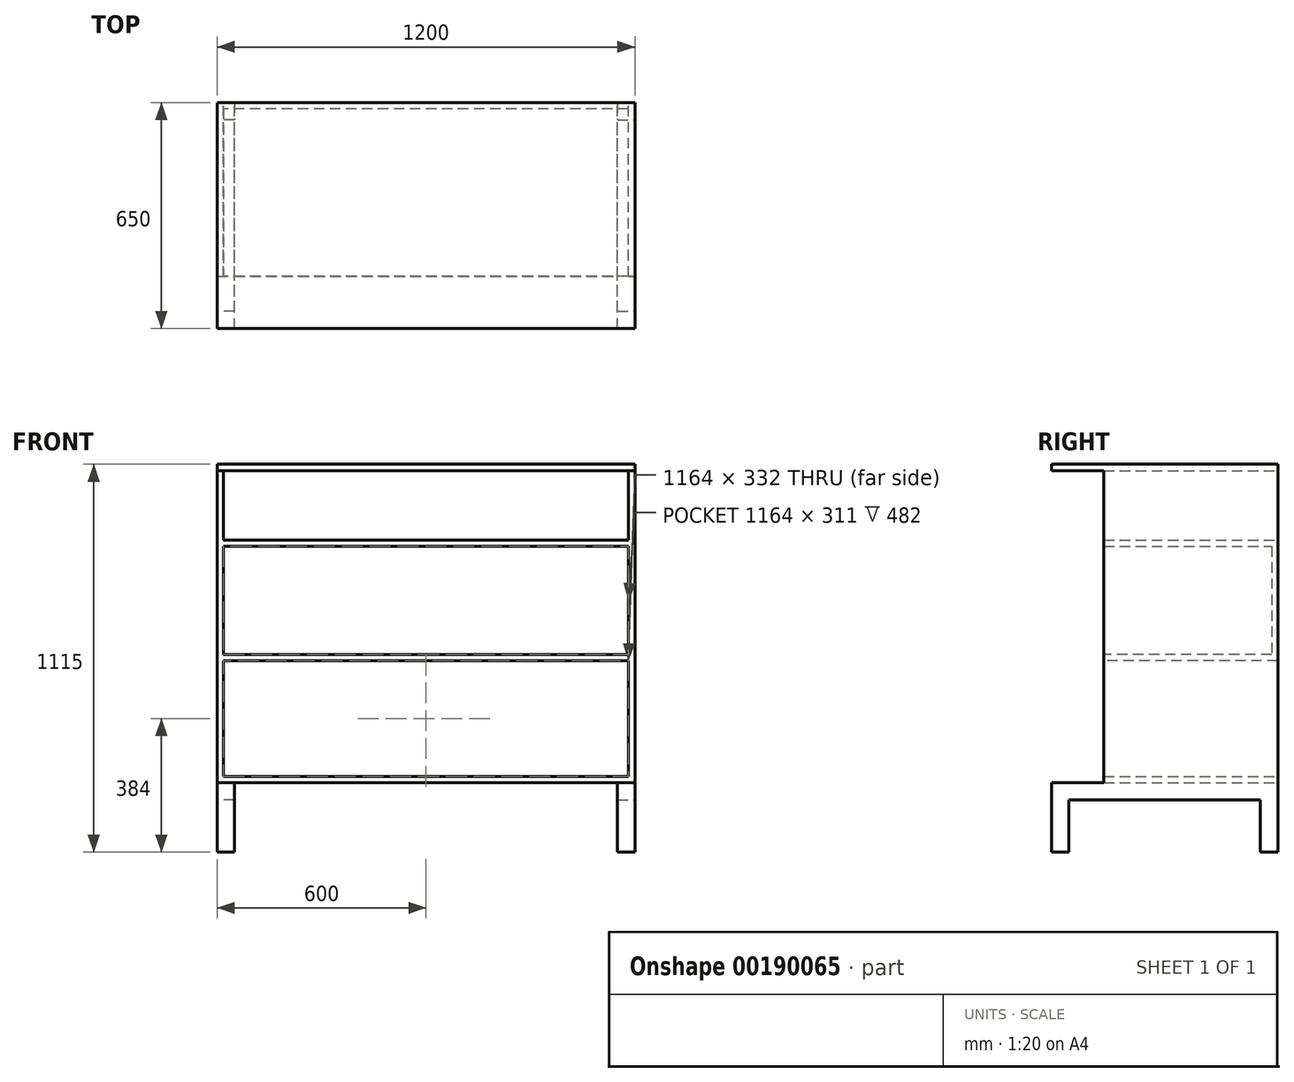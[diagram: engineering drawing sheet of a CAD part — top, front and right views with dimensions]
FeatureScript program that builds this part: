
annotation { "Feature Type Name" : "Feature", "Feature Type Description" : "" }
export const myFeature = defineFeature(function(context is Context, id is Id, definition is map)
    precondition{}
    {
        {
            var Q0;
            Q0=qCreatedBy(makeId("Front.planeOp"),FACE);
            var sketch = newSketch(context, id + "F0", { "sketchPlane" : qUnion([Q0])});
            skLineSegment(sketch, "E0.bottom", {"start": v(-600, 1115) * mm, "end": v(0, 1115) * mm});
            skLineSegment(sketch, "E0.left", {"start": v(-600, 1115) * mm, "end": v(-600, 200) * mm});
            skLineSegment(sketch, "E0.right", {"start": v(0, 1115) * mm, "end": v(0, 1097) * mm});
            skLineSegment(sketch, "E1", {"start": v(-600, 200) * mm, "end": v(0, 200) * mm});
            skLineSegment(sketch, "E2", {"start": v(0, 200) * mm, "end": v(0, 218) * mm});
            skLineSegment(sketch, "E3", {"start": v(0, 218) * mm, "end": v(-582, 218) * mm});
            skLineSegment(sketch, "E4", {"start": v(-582, 218) * mm, "end": v(-582, 1097) * mm});
            skLineSegment(sketch, "E5", {"start": v(-582, 1097) * mm, "end": v(0, 1097) * mm});
            skSolve(sketch);
        }
        {
            var Q0;
            Q0 = qSketchRegion(id + "F0", true);
            extrude(context, id + "F1", {"entities" : qUnion([Q0]), "depth" : 500 * mm});
        }
        {
            var Q0;
            Q0=qCreatedBy(makeId("Front.planeOp"),FACE);
            cPlane(context, id + "F2", {"entities" : qUnion([Q0]), "cplaneType" : CPlaneType.OFFSET, "offset" : 0 * mm, "oppositeDirection" : true, "width" : 150 * mm, "height" : 150 * mm});
        }
        {
            var Q0;
            Q0=qCreatedBy(id+"F2.planeOp",FACE);
            var sketch = newSketch(context, id + "F3", { "sketchPlane" : qUnion([Q0])});
            skLineSegment(sketch, "E6.bottom", {"start": v(-600, 200) * mm, "end": v(-550, 200) * mm});
            skLineSegment(sketch, "E6.top", {"start": v(-600, 150) * mm, "end": v(-550, 150) * mm});
            skLineSegment(sketch, "E6.left", {"start": v(-600, 200) * mm, "end": v(-600, 150) * mm});
            skLineSegment(sketch, "E6.right", {"start": v(-550, 200) * mm, "end": v(-550, 150) * mm});
            skSolve(sketch);
        }
        {
            var Q0;
            Q0 = qSketchRegion(id + "F3", true);
            extrude(context, id + "F4", {"entities" : qUnion([Q0]), "operationType" : NewBodyOperationType.ADD, "depth" : 650 * mm});
        }
        {
            var Q0;
            Q0=qCreatedBy(makeId("Top.planeOp"),FACE);
            var sketch = newSketch(context, id + "F5", { "sketchPlane" : qUnion([Q0])});
            skLineSegment(sketch, "E7.bottom", {"start": v(-600, 0) * mm, "end": v(-550, 0) * mm});
            skLineSegment(sketch, "E7.top", {"start": v(-600, -50) * mm, "end": v(-550, -50) * mm});
            skLineSegment(sketch, "E7.left", {"start": v(-600, 0) * mm, "end": v(-600, -50) * mm});
            skLineSegment(sketch, "E7.right", {"start": v(-550, 0) * mm, "end": v(-550, -50) * mm});
            skLineSegment(sketch, "E8.bottom", {"start": v(-600, -650) * mm, "end": v(-550, -650) * mm});
            skLineSegment(sketch, "E8.top", {"start": v(-600, -600) * mm, "end": v(-550, -600) * mm});
            skLineSegment(sketch, "E8.left", {"start": v(-600, -650) * mm, "end": v(-600, -600) * mm});
            skLineSegment(sketch, "E8.right", {"start": v(-550, -650) * mm, "end": v(-550, -600) * mm});
            skSolve(sketch);
        }
        {
            var Q0;
            Q0 = qSketchRegion(id + "F5", true);
            extrude(context, id + "F6", {"entities" : qUnion([Q0]), "operationType" : NewBodyOperationType.ADD, "depth" : 200 * mm});
        }
        {
            var Q0;
            Q0=makeQuery(id+"F1.opExtrude","SWEPT_BODY",BODY,{"disambiguationData":[OSD([sQuery(id+"F0.wireOp",EDGE,"E0.bottom"),sQuery(id+"F0.wireOp",EDGE,"E0.left"),sQuery(id+"F0.wireOp",EDGE,"E0.right"),sQuery(id+"F0.wireOp",EDGE,"E1"),sQuery(id+"F0.wireOp",EDGE,"E2"),sQuery(id+"F0.wireOp",EDGE,"E3"),sQuery(id+"F0.wireOp",EDGE,"E4"),sQuery(id+"F0.wireOp",EDGE,"E5")])]});
            var Q1;
            Q1=qCreatedBy(makeId("Right.planeOp"),FACE);
            mirror(context, id + "F7", {"operationType" : NewBodyOperationType.ADD, "entities" : qUnion([Q0]), "mirrorPlane" : qUnion([Q1])});
        }
        {
            var Q0;
            {var subQ0=makeQuery(id+"F1.opExtrude","CAP_FACE",FACE,{"disambiguationData":[OSD([sQuery(id+"F0.wireOp",EDGE,"E0.bottom"),sQuery(id+"F0.wireOp",EDGE,"E0.left"),sQuery(id+"F0.wireOp",EDGE,"E0.right"),sQuery(id+"F0.wireOp",EDGE,"E1"),sQuery(id+"F0.wireOp",EDGE,"E2"),sQuery(id+"F0.wireOp",EDGE,"E3"),sQuery(id+"F0.wireOp",EDGE,"E4"),sQuery(id+"F0.wireOp",EDGE,"E5")])],"isStart":false});Q0=makeQuery(id+"F7.boolean.opBoolean","MERGE",FACE,{"derivedFrom":[subQ0,makeQuery(id+"F7.opPattern","COPY",FACE,{"derivedFrom":subQ0,"instanceName":"1"})]});}
            var sketch = newSketch(context, id + "F8", { "sketchPlane" : qUnion([Q0])});
            skLineSegment(sketch, "E9.bottom", {"start": v(-600, 1115) * mm, "end": v(600, 1115) * mm});
            skLineSegment(sketch, "E9.top", {"start": v(-600, 1097) * mm, "end": v(600, 1097) * mm});
            skLineSegment(sketch, "E9.left", {"start": v(-600, 1115) * mm, "end": v(-600, 1097) * mm});
            skLineSegment(sketch, "E9.right", {"start": v(600, 1115) * mm, "end": v(600, 1097) * mm});
            skSolve(sketch);
        }
        {
            var Q0;
            Q0 = qSketchRegion(id + "F8", true);
            extrude(context, id + "F9", {"entities" : qUnion([Q0]), "operationType" : NewBodyOperationType.ADD, "depth" : 150 * mm});
        }
        {
            var Q0;
            Q0=makeQuery(id+"F1.opExtrude","SWEPT_FACE",FACE,{"disambiguationData":[OSD([sQuery(id+"F0.wireOp",EDGE,"E4")])]});
            var sketch = newSketch(context, id + "F10", { "sketchPlane" : qUnion([Q0])});
            skLineSegment(sketch, "E10", {"start": v(-500, 897) * mm, "end": v(0, 897) * mm});
            skLineSegment(sketch, "E11", {"start": v(0, 897) * mm, "end": v(0, 550) * mm});
            skLineSegment(sketch, "E12", {"start": v(0, 550) * mm, "end": v(-500, 550) * mm});
            skLineSegment(sketch, "E13.0", {"start": v(-18, 568) * mm, "end": v(-500, 568) * mm});
            skLineSegment(sketch, "E13.1", {"start": v(-18, 879) * mm, "end": v(-18, 568) * mm});
            skLineSegment(sketch, "E13.2", {"start": v(-500, 879) * mm, "end": v(-18, 879) * mm});
            skLineSegment(sketch, "E14", {"start": v(-500, 897) * mm, "end": v(-500, 879) * mm});
            skLineSegment(sketch, "E15", {"start": v(-500, 568) * mm, "end": v(-500, 550) * mm});
            skSolve(sketch);
        }
        {
            var Q0;
            Q0 = qSketchRegion(id + "F10", true);
            var Q1;
            Q1=makeQuery(id+"F7.opPattern","COPY",FACE,{"derivedFrom":makeQuery(id+"F1.opExtrude","SWEPT_FACE",FACE,{"disambiguationData":[OSD([sQuery(id+"F0.wireOp",EDGE,"E4")])]}),"instanceName":"1"});
            extrude(context, id + "F11", {"entities" : qUnion([Q0]), "operationType" : NewBodyOperationType.ADD, "endBound" : BoundingType.UP_TO_SURFACE, "endBoundEntityFace" : qUnion([Q1]), "depth" : 25 * mm});
        }
    });
